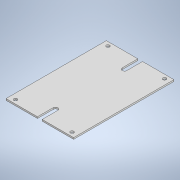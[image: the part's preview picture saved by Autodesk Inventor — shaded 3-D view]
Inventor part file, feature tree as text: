
AUTODESK INVENTOR PART (.ipt)
format: ipt  version: 2022 (Build 260153000, 153)  size: 165,376 bytes
history: native  units: in
note: dims shown in document units (in); Inventor stores cm internally (conversion verified against a paired STEP export)
features: sketch x3, extrude x2, hole x1
ambient origin geometry x8: Origin, YZ Plane, XZ Plane, XY Plane, X Axis, Y Axis, Z Axis, Center Point
bodies: Body1 (feature_tree)
feature tree (6):
  extrude  "Extrusion2"  Depth=1.6969in
  hole  "Hole1"  [1 undecoded]
  extrude  "Extrusion3"  Depth=0.0591in
  sketch  "Sketch2"  dims[d28=2.5197in d29=1.6969in]
  sketch  "Sketch3"  dims[d30=0.0394in d31=0.0in d32=2.3228in]
  sketch  "Sketch4"  dims[d33=1.1614in d34=1.4213in d35=0.7106in d36=0.0866in d37=0.2362in d38=0.1732in d39=0.0787in d40=0.6181in d41=0.315in d42=0.8108in d43=0.0591in d44=0.1181in d45=0.3937in d46=0.0591in d47=0.0in d48=0.0in]
note: 1 required parameter value undecoded (feature->parameter linkage not recoverable at this tier; creation-order binding heuristic only, values carry confidence <= 0.55)
